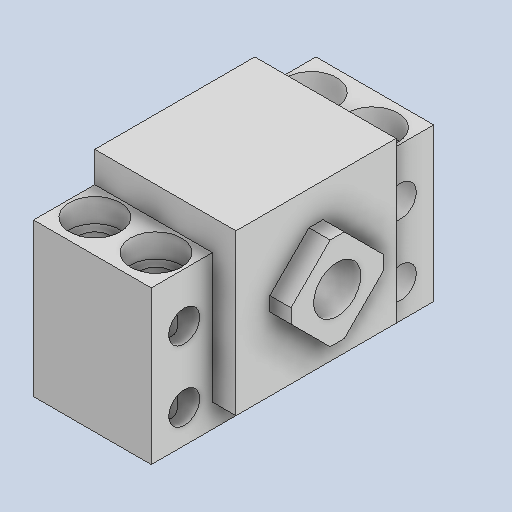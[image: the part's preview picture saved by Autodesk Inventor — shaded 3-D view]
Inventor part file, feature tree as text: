
AUTODESK INVENTOR PART (.ipt)
format: ipt  version: 2023 (Build 270158000, 158)  size: 239,104 bytes
history: native  units: mm
features: extrude x5, sketch x5, pattern_linear x1
ambient origin geometry x8: Origin, YZ Plane, XZ Plane, XY Plane, X Axis, Y Axis, Z Axis, Center Point
bodies: Solid1 (feature_tree)
feature tree (11):
  extrude  "Extrusion1"  Depth=60.0mm
  extrude  "Extrusion2"  Depth=46.0mm
  extrude  "Extrusion3"  Depth=32.5mm
  extrude  "Extrusion4"  Depth=39.0mm
  extrude  "Extrusion5"  Depth=25.0mm TaperAngle=0.0deg
  pattern_linear  "Rectangular Pattern1"  Spacing1=5.0mm  [1 undecoded]
  sketch  "Sketch1"  dims[d0=60.0mm d1=6.6mm]
  sketch  "Sketch2"  dims[d2=15.0mm d3=46.0mm]
  sketch  "Sketch3"  dims[d4=22.0mm d5=32.5mm]
  sketch  "Sketch4"  dims[d6=34.0mm d7=39.0mm]
  sketch  "Sketch5"  dims[d8=10.0mm d9=25.0mm d10=0.0mm d11=5.0mm d12=0.0mm d14=135.0deg d15=16.0mm d16=3.0mm d17=4.5mm d18=0.0mm d19=10.8mm d20=6.0mm d21=7.0mm d22=5.0mm d23=0.0mm d24=6.6mm d25=5.0mm d26=0.0mm d27=20.0mm d29=13.0mm d30=20.0mm d32=-46.0mm]
note: 1 required parameter value undecoded (feature->parameter linkage not recoverable at this tier; creation-order binding heuristic only, values carry confidence <= 0.55)
